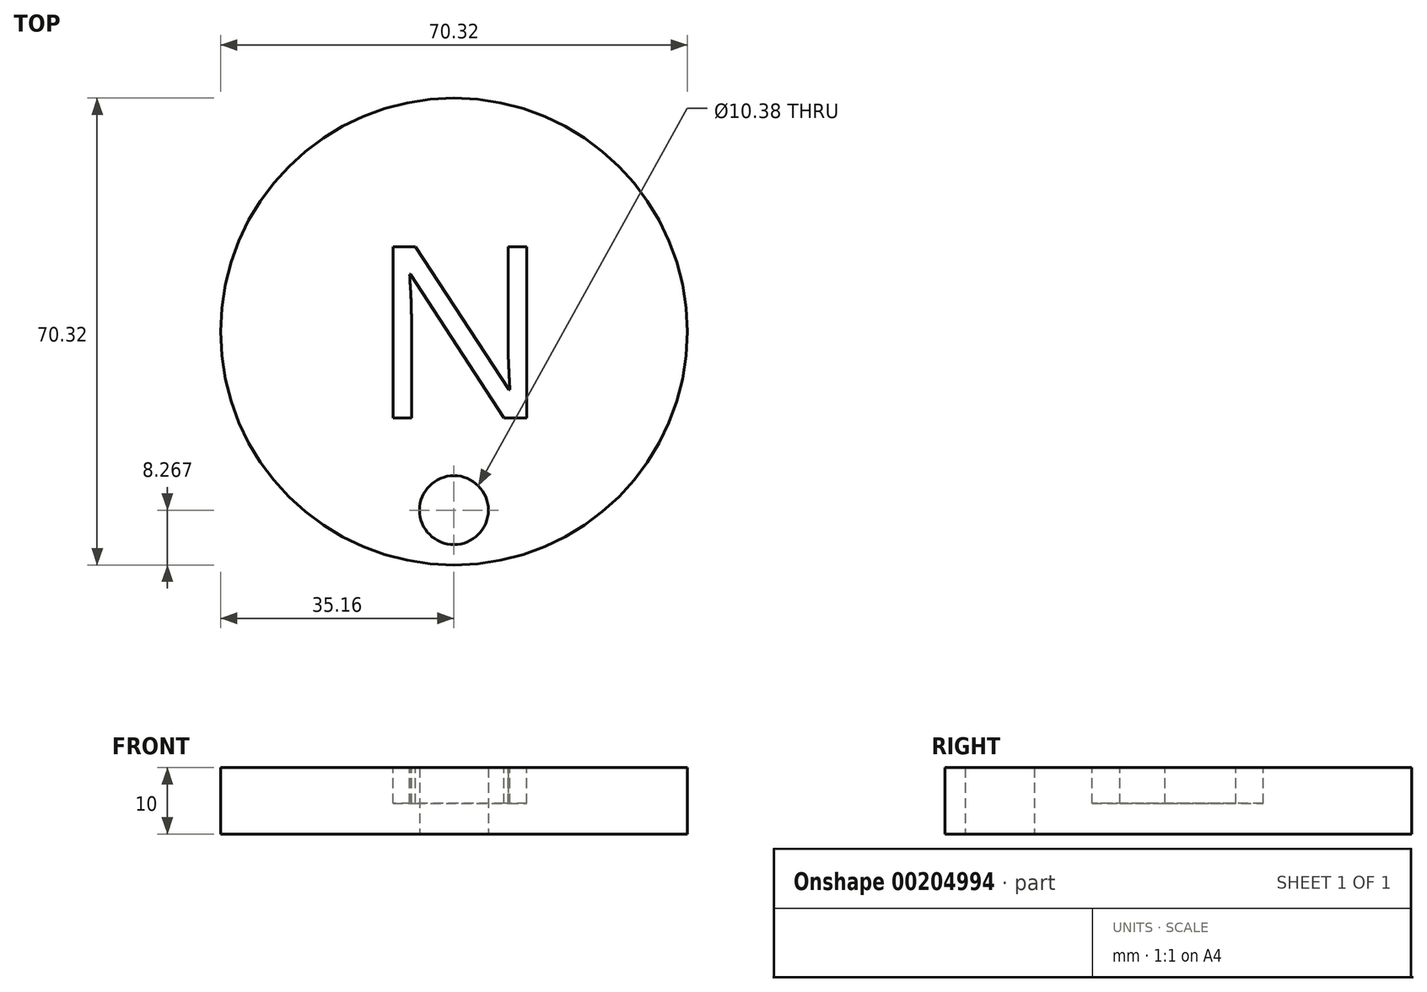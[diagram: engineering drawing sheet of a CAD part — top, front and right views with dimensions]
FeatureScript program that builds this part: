
annotation { "Feature Type Name" : "Feature", "Feature Type Description" : "" }
export const myFeature = defineFeature(function(context is Context, id is Id, definition is map)
    precondition{}
    {
        {
            var Q0;
            Q0=qCreatedBy(makeId("Top.planeOp"),FACE);
            var sketch = newSketch(context, id + "F0", { "sketchPlane" : qUnion([Q0])});
            skCircle(sketch, "E0", {"center": v(0, 0) * mm, "radius": 35.16 * mm});
            skSolve(sketch);
        }
        {
            var Q0;
            Q0 = qSketchRegion(id + "F0", true);
            extrude(context, id + "F1", {"entities" : qUnion([Q0]), "depth" : 10 * mm});
        }
        {
            var Q0;
            Q0=qCreatedBy(makeId("Top.planeOp"),FACE);
            var sketch = newSketch(context, id + "F2", { "sketchPlane" : qUnion([Q0])});
            skCircle(sketch, "E1", {"center": v(0, -26.9) * mm, "radius": 5.2 * mm});
            skSolve(sketch);
        }
        {
            var Q0;
            Q0 = qSketchRegion(id + "F2", true);
            extrude(context, id + "F3", {"entities" : qUnion([Q0]), "operationType" : NewBodyOperationType.REMOVE, "depth" : 66.4 * mm});
        }
        {
            var Q0;
            Q0=makeQuery(id+"F1.opExtrude","CAP_FACE",FACE,{"disambiguationData":[OSD([sQuery(id+"F0.wireOp",EDGE,"E0")])],"isStart":false});
            var sketch = newSketch(context, id + "F4", { "sketchPlane" : qUnion([Q0])});
            skText(sketch, "E2", { "text": "N", "fontName": "OpenSans-Regular.ttf"});
            const initialGuessF4  = {"E2": [-0.01272, -0.01301, 1, 0, 0.02603]};
            skSetInitialGuess(sketch, initialGuessF4);
            skSolve(sketch);
        }
        {
            var Q0;
            Q0 = qSketchRegion(id + "F4", true);
            extrude(context, id + "F5", {"entities" : qUnion([Q0]), "operationType" : NewBodyOperationType.REMOVE, "oppositeDirection" : true, "depth" : 5.4 * mm});
        }
    });
